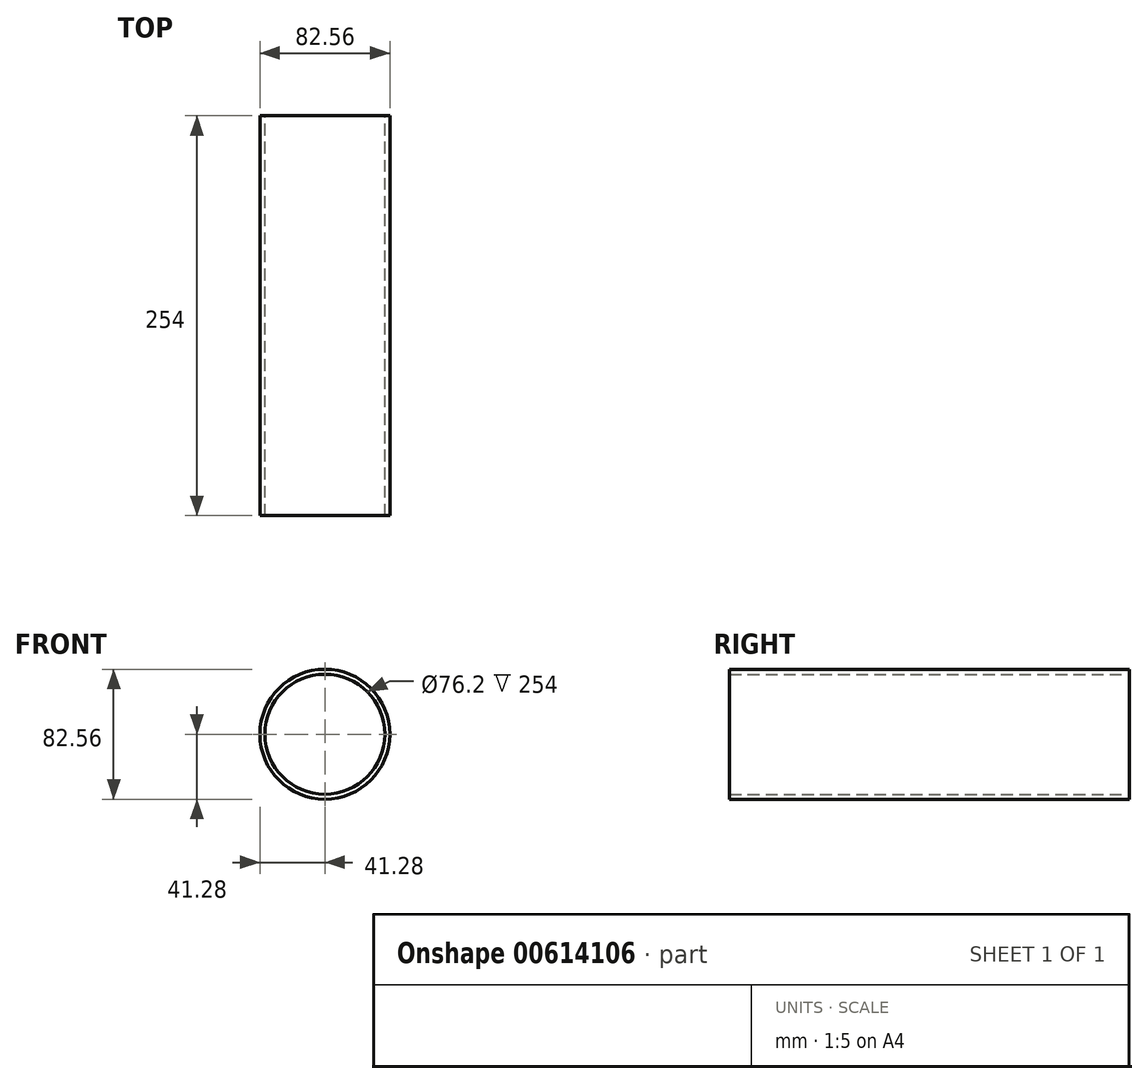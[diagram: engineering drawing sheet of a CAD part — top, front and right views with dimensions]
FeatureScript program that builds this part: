
annotation { "Feature Type Name" : "Feature", "Feature Type Description" : "" }
export const myFeature = defineFeature(function(context is Context, id is Id, definition is map)
    precondition{}
    {
        {
            var Q0;
            Q0=qCreatedBy(makeId("Front.planeOp"),FACE);
            var sketch = newSketch(context, id + "F0", { "sketchPlane" : qUnion([Q0])});
            skCircle(sketch, "E0", {"center": v(0, 0) * mm, "radius": 41.28 * mm});
            skCircle(sketch, "E1", {"center": v(0, 0) * mm, "radius": 38.1 * mm});
            skSolve(sketch);
        }
        {
            var Q0;
            Q0 = qSketchRegion(id + "F0", true);
            extrude(context, id + "F1", {"entities" : qUnion([Q0]), "depth" : 254 * mm, "offsetDistance" : 25.4 * mm});
        }
    });
